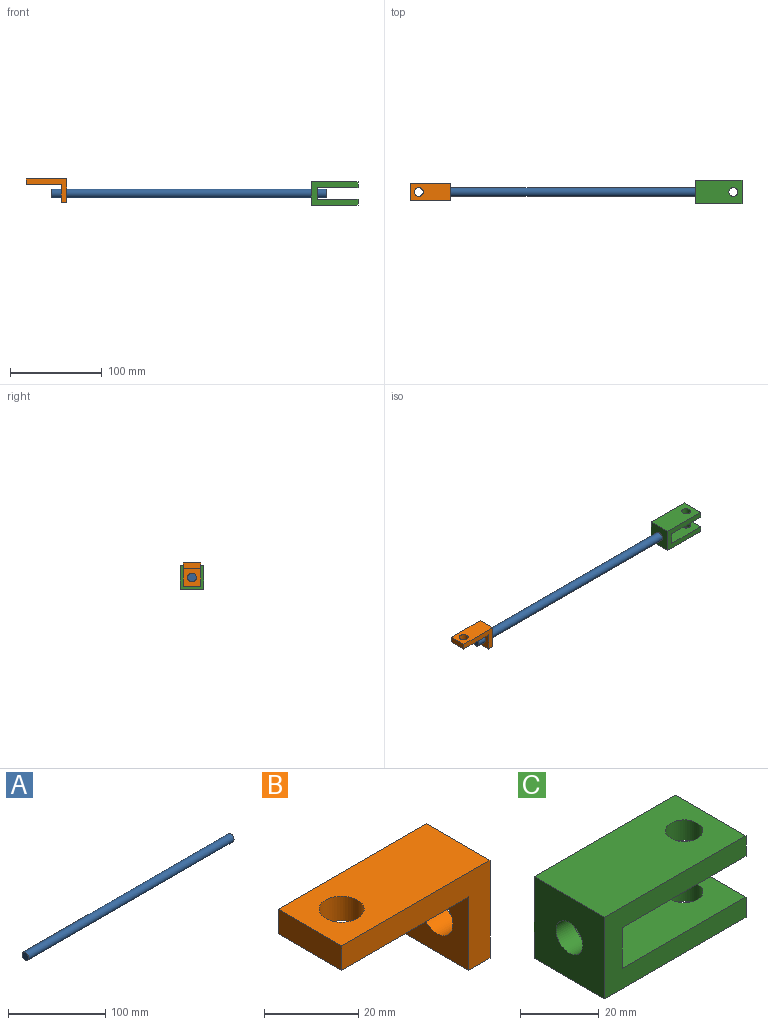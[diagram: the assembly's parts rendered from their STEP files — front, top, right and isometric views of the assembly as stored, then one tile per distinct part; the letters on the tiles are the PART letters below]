
ASSEMBLY  parts=3 mates=2
PART A: 3 faces, bbox 298.5x9.5x9.5 mm
  f0: cylinder r=4.76mm len=298.45mm, axis (-1,0,0), area 8930.7mm2, adj f1,f2
  f1: plane 9.53x9.53mm, normal (1,0,0), area 71.3mm2, adj f0
  f2: plane 9.53x9.53mm, normal (-1,0,0), area 71.3mm2, adj f0
PART B: 10 faces, bbox 44.5x19.1x25.4 mm
  f0: plane 38.1x19.05mm, normal (0,0,-1), area 654.5mm2, adj f1,f5,f6,f7,f9
  f1: plane 19.05x19.05mm, normal (-1,0,0), area 291.6mm2, adj f0,f2,f6,f7,f8
  f2: plane 19.05x6.35mm, normal (0,0,-1), area 121mm2, adj f1,f3,f6,f7
  f3: plane 25.4x19.05mm, normal (1,0,0), area 412.6mm2, adj f2,f4,f6,f7,f8
  f4: plane 44.45x19.05mm, normal (0,0,1), area 775.5mm2, adj f3,f5,f6,f7,f9
  f5: plane 19.05x6.35mm, normal (-1,0,0), area 121mm2, adj f0,f4,f6,f7
  f6: plane 44.45x25.4mm, normal (0,-1,0), area 403.2mm2, adj f0,f1,f2,f3,f4,f5
  f7: plane 44.45x25.4mm, normal (0,1,0), area 403.2mm2, adj f0,f1,f2,f3,f4,f5
  f8: cylinder r=4.76mm len=9.53mm, axis (-1,0,0), area 190mm2, adj f1,f3
  f9: cylinder r=4.76mm len=9.53mm, axis (0,0,1), area 190mm2, adj f0,f4
PART C: 13 faces, bbox 50.8x25.4x25.4 mm
  f0: plane 50.8x25.4mm, normal (0,0,1), area 1219.1mm2, adj f1,f7,f8,f9,f11
  f1: plane 25.4x25.4mm, normal (-1,0,0), area 573.9mm2, adj f0,f2,f8,f9,f10
  f2: plane 50.8x25.4mm, normal (0,0,-1), area 1219.1mm2, adj f1,f3,f8,f9,f12
  f3: plane 25.4x6.35mm, normal (1,0,0), area 161.3mm2, adj f2,f4,f8,f9
  f4: plane 44.45x25.4mm, normal (0,0,1), area 1057.8mm2, adj f3,f5,f8,f9,f12
  f5: plane 25.4x12.7mm, normal (1,0,0), area 251.3mm2, adj f4,f6,f8,f9,f10
  f6: plane 44.45x25.4mm, normal (0,0,-1), area 1057.8mm2, adj f5,f7,f8,f9,f11
  f7: plane 25.4x6.35mm, normal (1,0,0), area 161.3mm2, adj f0,f6,f8,f9
  f8: plane 50.8x25.4mm, normal (0,-1,0), area 725.8mm2, adj f0,f1,f2,f3,f4,f5,f6,f7
  f9: plane 50.8x25.4mm, normal (0,1,0), area 725.8mm2, adj f0,f1,f2,f3,f4,f5,f6,f7
  f10: cylinder r=4.76mm len=9.53mm, axis (-1,0,0), area 190mm2, adj f1,f5
  f11: cylinder r=4.76mm len=9.53mm, axis (0,0,1), area 190mm2, adj f0,f6
  f12: cylinder r=4.76mm len=9.53mm, axis (0,0,1), area 190mm2, adj f2,f4
PLACE A at identity fixed
PLACE B t=(10,0,0)mm
PLACE C t=(-10,0,0)mm
MATE revolute A.f0 <-> C.f10  axis (-1,0,0) through (298.45,0,0)mm
MATE revolute B.f8 <-> A.f0  axis (-1,0,0) through (10,0,0)mm
